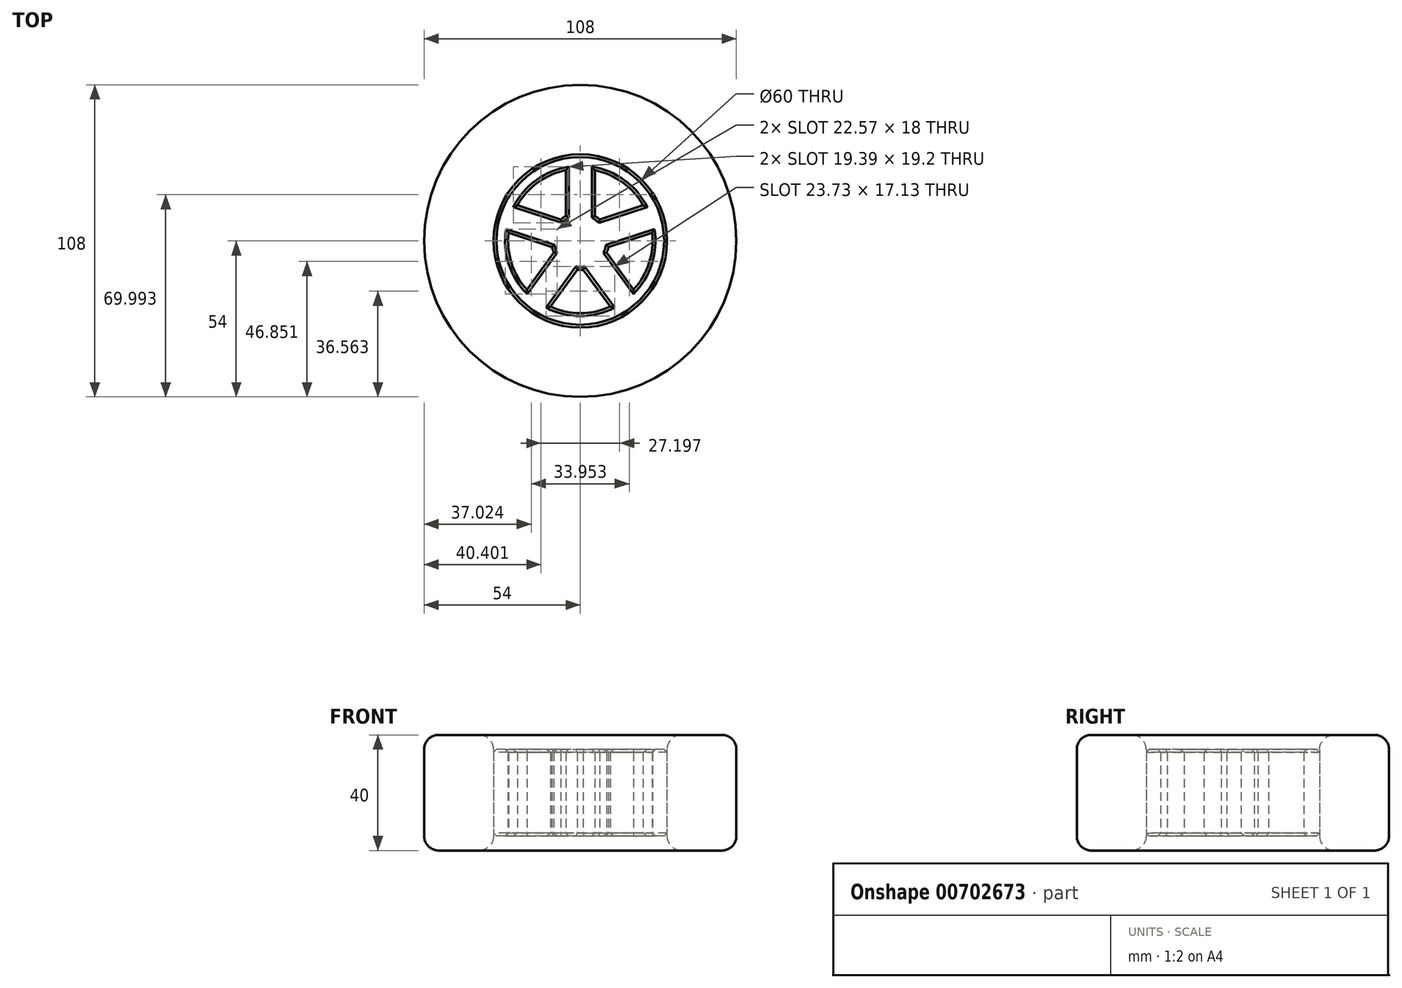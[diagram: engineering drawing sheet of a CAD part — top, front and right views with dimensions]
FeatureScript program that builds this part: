
annotation { "Feature Type Name" : "Feature", "Feature Type Description" : "" }
export const myFeature = defineFeature(function(context is Context, id is Id, definition is map)
    precondition{}
    {
        {
            var Q0;
            Q0=qCreatedBy(makeId("Top.planeOp"),FACE);
            var sketch = newSketch(context, id + "F0", { "sketchPlane" : qUnion([Q0])});
            skCircle(sketch, "E0", {"center": v(0, 0) * mm, "radius": 54 * mm});
            skArc(sketch, "E1", {"start": v(-24.84, 2.81) * mm, "mid": v(-14.7, -20.23) * mm, "end": v(10.35, -22.76) * mm});
            skArc(sketch, "E2", {"start": v(-9.78, -2.08) * mm, "mid": v(-9.51, -3.1) * mm, "end": v(-9.14, -4.07) * mm});
            skCircle(sketch, "E3", {"center": v(0, 0) * mm, "radius": 30 * mm});
            skLineSegment(sketch, "E4", {"start": v(-5, 8.66) * mm, "end": v(-5, 24.5) * mm});
            skLineSegment(sketch, "E5", {"start": v(5, 8.66) * mm, "end": v(5, 24.5) * mm});
            skLineSegment(sketch, "E6.1.0", {"start": v(-9.78, -2.08) * mm, "end": v(-24.84, 2.81) * mm});
            skLineSegment(sketch, "E6.1.1", {"start": v(-6.7, 7.43) * mm, "end": v(-21.75, 12.32) * mm});
            skLineSegment(sketch, "E6.2.0", {"start": v(-1.05, -9.95) * mm, "end": v(-10.35, -22.76) * mm});
            skLineSegment(sketch, "E6.2.1", {"start": v(-9.14, -4.07) * mm, "end": v(-18.44, -16.88) * mm});
            skLineSegment(sketch, "E7.1.3.0", {"start": v(9.14, -4.07) * mm, "end": v(18.44, -16.88) * mm});
            skLineSegment(sketch, "E7.3.3.0", {"start": v(1.05, -9.95) * mm, "end": v(10.35, -22.76) * mm});
            skLineSegment(sketch, "E7.1.4.0", {"start": v(6.7, 7.43) * mm, "end": v(21.75, 12.32) * mm});
            skLineSegment(sketch, "E7.3.4.0", {"start": v(9.78, -2.08) * mm, "end": v(24.84, 2.81) * mm});
            skArc(sketch, "E8.trimOffspring", {"start": v(-5, 24.5) * mm, "mid": v(-14.7, 20.23) * mm, "end": v(-21.75, 12.32) * mm});
            skArc(sketch, "E9.trimOffspring", {"start": v(-5, 8.66) * mm, "mid": v(-5.88, 8.1) * mm, "end": v(-6.7, 7.43) * mm});
            skArc(sketch, "E10.trimOffspring", {"start": v(6.7, 7.43) * mm, "mid": v(5.88, 8.1) * mm, "end": v(5, 8.66) * mm});
            skArc(sketch, "E11.trimOffspring", {"start": v(9.14, -4.07) * mm, "mid": v(9.51, -3.1) * mm, "end": v(9.78, -2.08) * mm});
            skArc(sketch, "E12.trimOffspring", {"start": v(-1.05, -9.95) * mm, "mid": v(0, -10) * mm, "end": v(1.05, -9.95) * mm});
            skArc(sketch, "E13.trimOffspring", {"start": v(21.75, 12.32) * mm, "mid": v(14.7, 20.23) * mm, "end": v(5, 24.5) * mm});
            skArc(sketch, "E14.trimOffspring", {"start": v(18.44, -16.88) * mm, "mid": v(23.78, -7.73) * mm, "end": v(24.84, 2.81) * mm});
            skSolve(sketch);
        }
        {
            var Q0;
            Q0=makeQuery(id+"F0.imprint","IMPRINT",FACE,{"disambiguationData":[TD([[makeQuery(id+"F0.imprint","IMPRINT",EDGE,{"derivedFrom":sQuery(id+"F0.wireOp",EDGE,"E0")}),1.0]])]});
            extrude(context, id + "F1", {"entities" : qUnion([Q0]), "depth" : 40 * mm, "offsetDistance" : 25 * mm});
        }
        {
            var Q0;
            Q0=makeQuery(id+"F0.imprint","IMPRINT",FACE,{"disambiguationData":[TD([[makeQuery(id+"F0.imprint","IMPRINT",EDGE,{"derivedFrom":sQuery(id+"F0.wireOp",EDGE,"E2")}),1.0]])]});
            extrude(context, id + "F2", {"entities" : qUnion([Q0]), "depth" : 35 * mm, "offsetDistance" : 25 * mm, "hasSecondDirection" : true, "secondDirectionOppositeDirection" : false, "secondDirectionDepth" : 5 * mm});
        }
        {
            var Q0;
            Q0=makeQuery(id+"F1.opExtrude","CAP_EDGE",EDGE,{"disambiguationData":[OSD([sQuery(id+"F0.wireOp",EDGE,"E0")])],"isStart":false});
            var Q1;
            Q1=makeQuery(id+"F1.opExtrude","CAP_EDGE",EDGE,{"disambiguationData":[OSD([sQuery(id+"F0.wireOp",EDGE,"E0")])],"isStart":true});
            var Q2;
            Q2=makeQuery(id+"F1.opExtrude","CAP_EDGE",EDGE,{"disambiguationData":[OSD([sQuery(id+"F0.wireOp",EDGE,"E3")])],"isStart":false});
            var Q3;
            Q3=makeQuery(id+"F1.opExtrude","CAP_EDGE",EDGE,{"disambiguationData":[OSD([sQuery(id+"F0.wireOp",EDGE,"E3")])],"isStart":true});
            fillet(context, id + "F3", {"entities" : qUnion([Q0, Q1, Q2, Q3]), "radius" : 5 * mm, "tangentPropagation" : true, "allowEdgeOverflow" : false});
        }
        {
            var Q0;
            Q0=makeQuery(id+"F2.opExtrude","CAP_FACE",FACE,{"disambiguationData":[OSD([sQuery(id+"F0.wireOp",EDGE,"E1"),sQuery(id+"F0.wireOp",EDGE,"E2"),sQuery(id+"F0.wireOp",EDGE,"E3"),sQuery(id+"F0.wireOp",EDGE,"E4"),sQuery(id+"F0.wireOp",EDGE,"E5"),sQuery(id+"F0.wireOp",EDGE,"E6.1.0"),sQuery(id+"F0.wireOp",EDGE,"E6.1.1"),sQuery(id+"F0.wireOp",EDGE,"E6.2.0"),sQuery(id+"F0.wireOp",EDGE,"E6.2.1"),sQuery(id+"F0.wireOp",EDGE,"E7.1.3.0"),sQuery(id+"F0.wireOp",EDGE,"E7.3.3.0"),sQuery(id+"F0.wireOp",EDGE,"E7.1.4.0"),sQuery(id+"F0.wireOp",EDGE,"E7.3.4.0"),sQuery(id+"F0.wireOp",EDGE,"E8.trimOffspring"),sQuery(id+"F0.wireOp",EDGE,"E9.trimOffspring"),sQuery(id+"F0.wireOp",EDGE,"E10.trimOffspring"),sQuery(id+"F0.wireOp",EDGE,"E11.trimOffspring"),sQuery(id+"F0.wireOp",EDGE,"E12.trimOffspring"),sQuery(id+"F0.wireOp",EDGE,"E13.trimOffspring"),sQuery(id+"F0.wireOp",EDGE,"E14.trimOffspring")])],"isStart":false});
            var Q1;
            Q1=makeQuery(id+"F2.opExtrude","CAP_FACE",FACE,{"disambiguationData":[OSD([sQuery(id+"F0.wireOp",EDGE,"E1"),sQuery(id+"F0.wireOp",EDGE,"E2"),sQuery(id+"F0.wireOp",EDGE,"E3"),sQuery(id+"F0.wireOp",EDGE,"E4"),sQuery(id+"F0.wireOp",EDGE,"E5"),sQuery(id+"F0.wireOp",EDGE,"E6.1.0"),sQuery(id+"F0.wireOp",EDGE,"E6.1.1"),sQuery(id+"F0.wireOp",EDGE,"E6.2.0"),sQuery(id+"F0.wireOp",EDGE,"E6.2.1"),sQuery(id+"F0.wireOp",EDGE,"E7.1.3.0"),sQuery(id+"F0.wireOp",EDGE,"E7.3.3.0"),sQuery(id+"F0.wireOp",EDGE,"E7.1.4.0"),sQuery(id+"F0.wireOp",EDGE,"E7.3.4.0"),sQuery(id+"F0.wireOp",EDGE,"E8.trimOffspring"),sQuery(id+"F0.wireOp",EDGE,"E9.trimOffspring"),sQuery(id+"F0.wireOp",EDGE,"E10.trimOffspring"),sQuery(id+"F0.wireOp",EDGE,"E11.trimOffspring"),sQuery(id+"F0.wireOp",EDGE,"E12.trimOffspring"),sQuery(id+"F0.wireOp",EDGE,"E13.trimOffspring"),sQuery(id+"F0.wireOp",EDGE,"E14.trimOffspring")])],"isStart":true});
            chamfer(context, id + "F4", {"entities" : qUnion([Q0, Q1]), "width" : 1 * mm, "tangentPropagation" : true});
        }
    });
